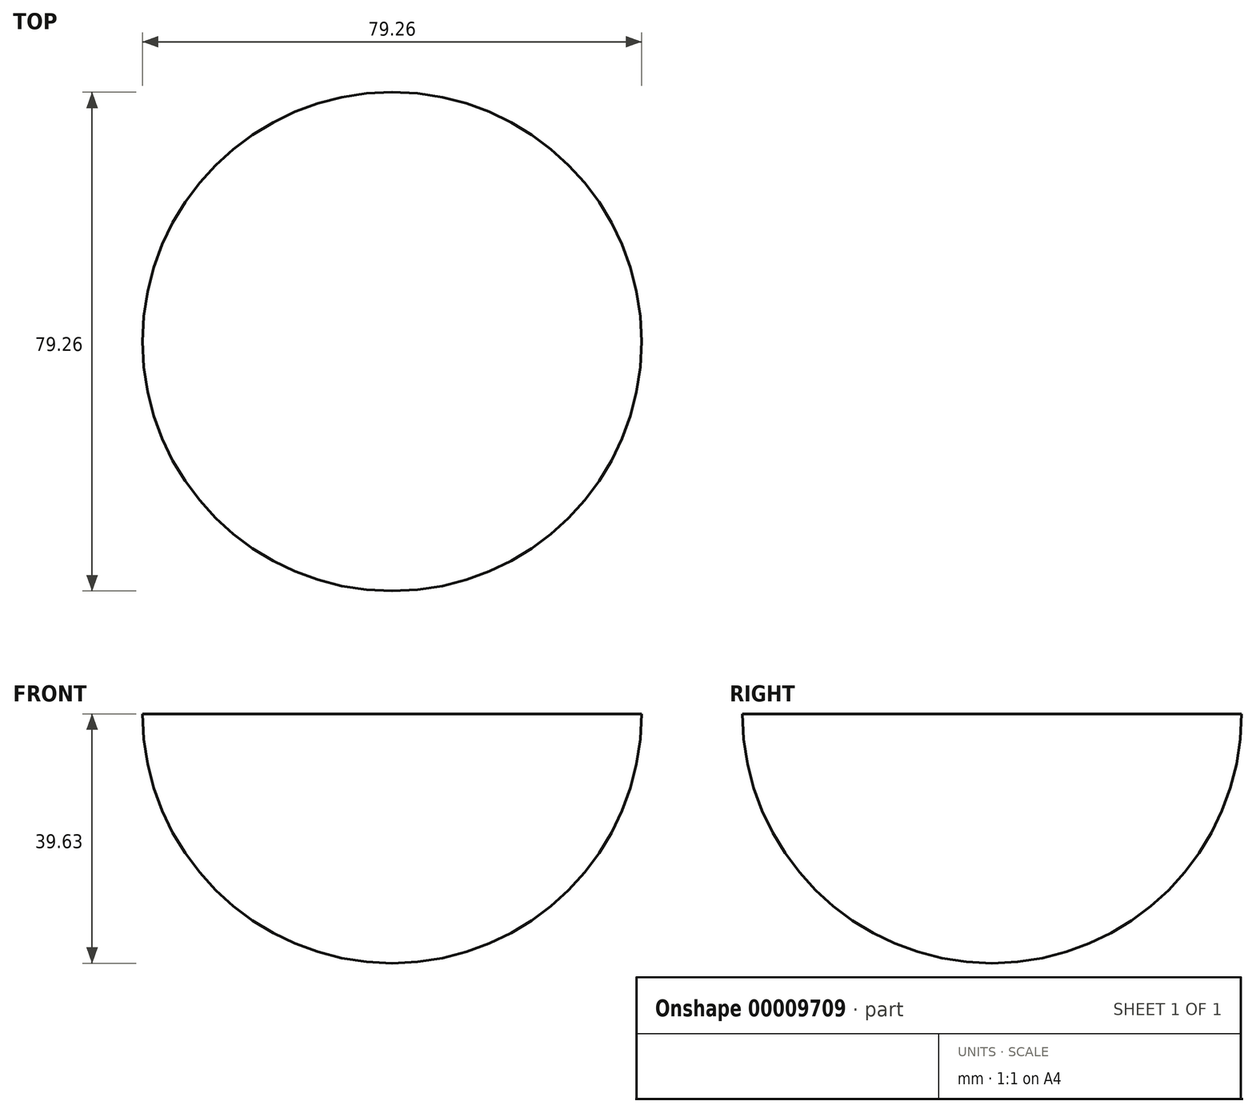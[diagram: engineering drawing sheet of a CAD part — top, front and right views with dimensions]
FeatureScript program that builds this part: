
annotation { "Feature Type Name" : "Feature", "Feature Type Description" : "" }
export const myFeature = defineFeature(function(context is Context, id is Id, definition is map)
    precondition{}
    {
        {
            var Q0;
            Q0=qCreatedBy(makeId("Top.planeOp"),FACE);
            var sketch = newSketch(context, id + "F0", { "sketchPlane" : qUnion([Q0])});
            skArc(sketch, "E0", {"start": v(0, 39.63) * mm, "mid": v(-39.63, 0) * mm, "end": v(0, -39.63) * mm});
            skLineSegment(sketch, "E1", {"start": v(0, -39.63) * mm, "end": v(0, 39.63) * mm});
            skSolve(sketch);
        }
        {
            var Q0;
            Q0 = qSketchRegion(id + "F0", true);
            var Q1;
            Q1=sQuery(id+"F0.wireOp",EDGE,"E1");
            revolve(context, id + "F1", {"entities" : qUnion([Q0]), "axis" : qUnion([Q1]), "revolveType" : RevolveType.ONE_DIRECTION, "oppositeDirection" : true, "angle" : 180 * degree});
        }
    });
